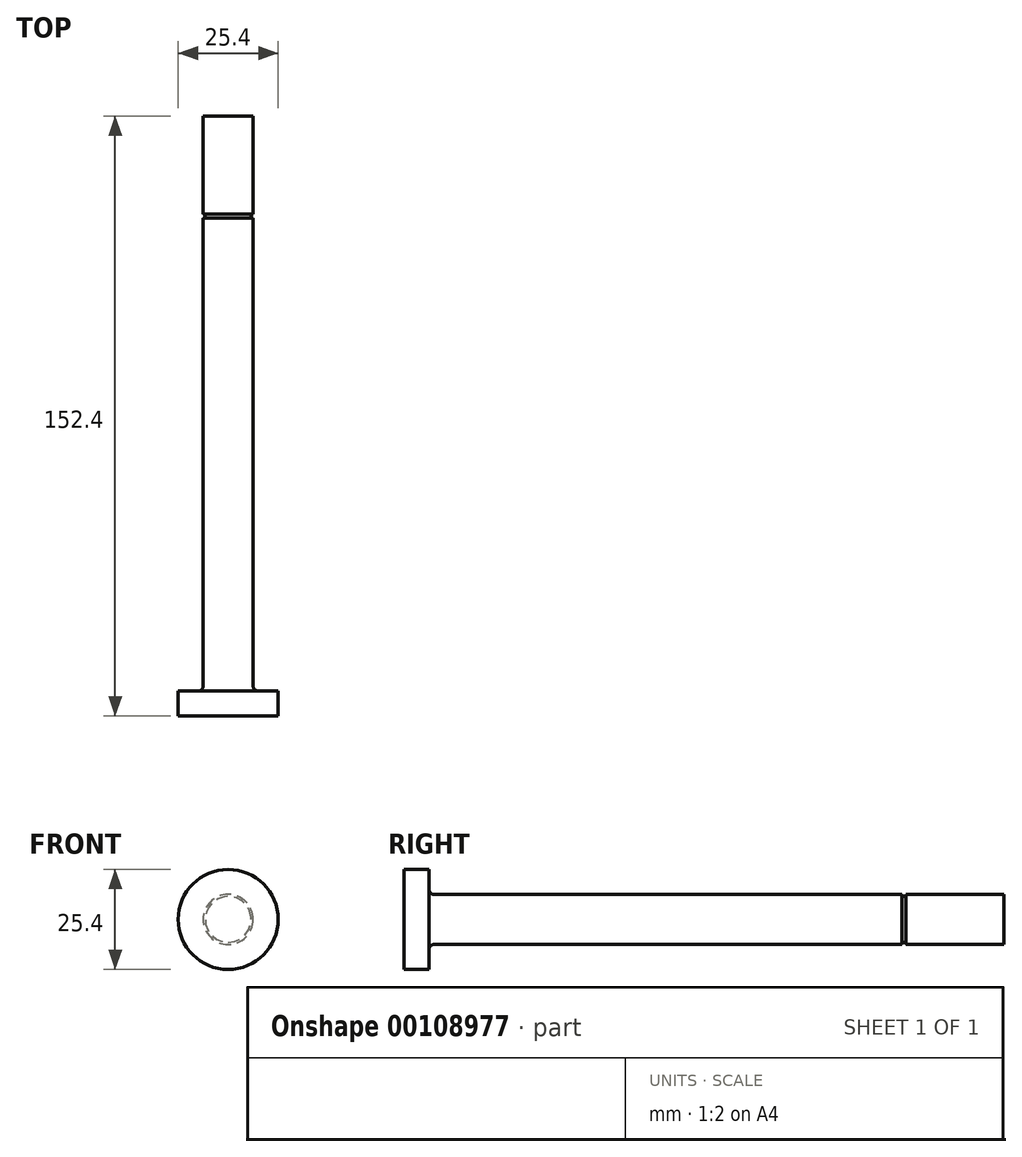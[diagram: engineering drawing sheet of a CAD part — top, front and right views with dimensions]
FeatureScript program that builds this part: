
annotation { "Feature Type Name" : "Feature", "Feature Type Description" : "" }
export const myFeature = defineFeature(function(context is Context, id is Id, definition is map)
    precondition{}
    {
        {
            var Q0;
            Q0=qCreatedBy(makeId("Right.planeOp"),FACE);
            var sketch = newSketch(context, id + "F0", { "sketchPlane" : qUnion([Q0])});
            skLineSegment(sketch, "E0.bottom", {"start": v(-36.76, 0) * mm, "end": v(109.3, 0) * mm});
            skLineSegment(sketch, "E0.top", {"start": v(-36.76, 6.35) * mm, "end": v(83.39, 6.35) * mm});
            skLineSegment(sketch, "E0.left", {"start": v(-36.76, 0) * mm, "end": v(-36.76, 6.35) * mm});
            skLineSegment(sketch, "E0.right", {"start": v(109.3, 0) * mm, "end": v(109.3, 6.35) * mm});
            skLineSegment(sketch, "E1.bottom", {"start": v(-36.76, 0) * mm, "end": v(-43.1, 0) * mm});
            skLineSegment(sketch, "E1.top", {"start": v(-36.76, 12.7) * mm, "end": v(-43.1, 12.7) * mm});
            skLineSegment(sketch, "E1.left", {"start": v(-36.76, 0) * mm, "end": v(-36.76, 12.7) * mm});
            skLineSegment(sketch, "E1.right", {"start": v(-43.1, 0) * mm, "end": v(-43.1, 12.7) * mm});
            skLineSegment(sketch, "E2", {"start": v(109.3, 6.35) * mm, "end": v(84.4, 6.35) * mm});
            skArc(sketch, "E3", {"start": v(83.39, 6.35) * mm, "mid": v(83.9, 5.84) * mm, "end": v(84.4, 6.35) * mm});
            skLineSegment(sketch, "E4.trimOffspring", {"start": v(84.4, 6.35) * mm, "end": v(109.3, 6.35) * mm});
            skSolve(sketch);
        }
        {
            var Q0;
            {var subQ3=sQuery(id+"F0.wireOp",EDGE,"E1.bottom");Q0=makeQuery(id+"F0.imprint","IMPRINT",FACE,{"disambiguationData":[TD([[makeQuery(id+"F0.imprint","IMPRINT",EDGE,{"derivedFrom":subQ3}),-1.0]])]});}
            var Q1;
            {var subQ1=sQuery(id+"F0.wireOp",EDGE,"E0.bottom");Q1=makeQuery(id+"F0.imprint","IMPRINT",FACE,{"disambiguationData":[TD([[makeQuery(id+"F0.imprint","IMPRINT",EDGE,{"derivedFrom":subQ1}),1.0]])]});}
            var Q2;
            Q2=sQuery(id+"F0.wireOp",EDGE,"E0.bottom");
            revolve(context, id + "F1", {"entities" : qUnion([Q0, Q1]), "axis" : qUnion([Q2]), "revolveType" : RevolveType.FULL});
        }
        {
            var Q0;
            Q0=makeQuery(id+"F1.opRevolve","SWEPT_EDGE",EDGE,{"disambiguationData":[OSD([sQuery(id+"F0.wireOp",EDGE,"E0.top"),sQuery(id+"F0.wireOp",EDGE,"E1.left")])]});
            fillet(context, id + "F2", {"entities" : qUnion([Q0]), "radius" : 1.27 * mm, "tangentPropagation" : true, "allowEdgeOverflow" : false});
        }
    });
